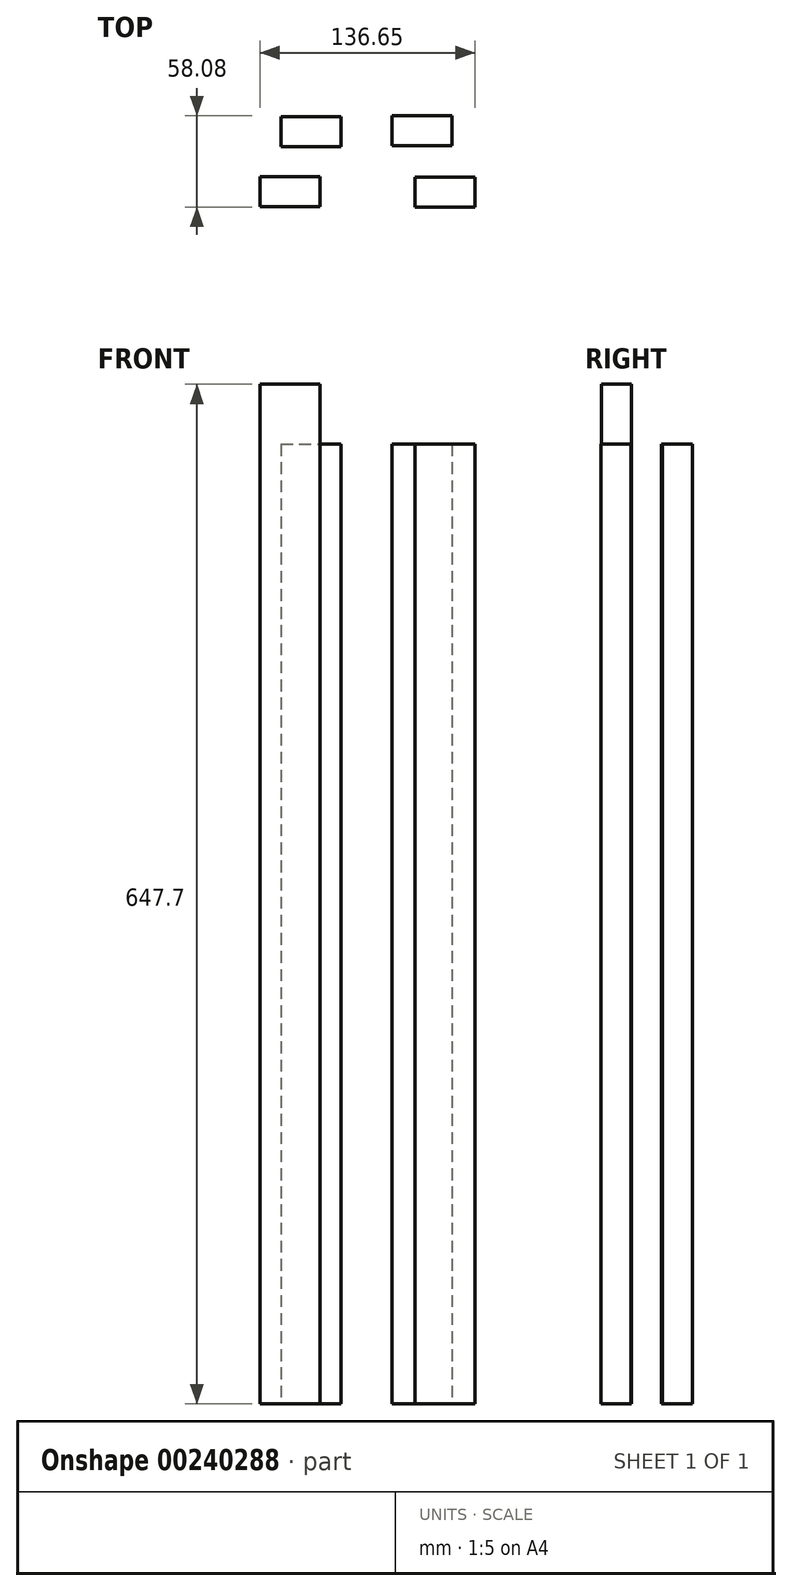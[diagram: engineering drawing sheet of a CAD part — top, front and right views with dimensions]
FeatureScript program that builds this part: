
annotation { "Feature Type Name" : "Feature", "Feature Type Description" : "" }
export const myFeature = defineFeature(function(context is Context, id is Id, definition is map)
    precondition{}
    {
        {
            var Q0;
            Q0=qCreatedBy(makeId("Top.planeOp"),FACE);
            var sketch = newSketch(context, id + "F0", { "sketchPlane" : qUnion([Q0])});
            skLineSegment(sketch, "E0.bottom", {"start": v(-65.46, 44.77) * mm, "end": v(-27.36, 44.77) * mm});
            skLineSegment(sketch, "E0.top", {"start": v(-65.46, 25.72) * mm, "end": v(-27.36, 25.72) * mm});
            skLineSegment(sketch, "E0.left", {"start": v(-65.46, 44.77) * mm, "end": v(-65.46, 25.72) * mm});
            skLineSegment(sketch, "E0.right", {"start": v(-27.36, 44.77) * mm, "end": v(-27.36, 25.72) * mm});
            skLineSegment(sketch, "E1.bottom", {"start": v(-78.98, 6.61) * mm, "end": v(-40.88, 6.61) * mm});
            skLineSegment(sketch, "E1.top", {"start": v(-78.98, -12.44) * mm, "end": v(-40.88, -12.44) * mm});
            skLineSegment(sketch, "E1.left", {"start": v(-78.98, 6.61) * mm, "end": v(-78.98, -12.44) * mm});
            skLineSegment(sketch, "E1.right", {"start": v(-40.88, 6.61) * mm, "end": v(-40.88, -12.44) * mm});
            skLineSegment(sketch, "E2.bottom", {"start": v(4.97, 45.36) * mm, "end": v(43.07, 45.36) * mm});
            skLineSegment(sketch, "E2.top", {"start": v(4.97, 26.3) * mm, "end": v(43.07, 26.3) * mm});
            skLineSegment(sketch, "E2.left", {"start": v(4.97, 45.36) * mm, "end": v(4.97, 26.3) * mm});
            skLineSegment(sketch, "E2.right", {"start": v(43.07, 45.36) * mm, "end": v(43.07, 26.3) * mm});
            skLineSegment(sketch, "E3.bottom", {"start": v(19.57, 6.33) * mm, "end": v(57.67, 6.33) * mm});
            skLineSegment(sketch, "E3.top", {"start": v(19.57, -12.72) * mm, "end": v(57.67, -12.72) * mm});
            skLineSegment(sketch, "E3.left", {"start": v(19.57, 6.33) * mm, "end": v(19.57, -12.72) * mm});
            skLineSegment(sketch, "E3.right", {"start": v(57.67, 6.33) * mm, "end": v(57.67, -12.72) * mm});
            skSolve(sketch);
        }
        {
            var Q0;
            Q0=makeQuery(id+"F0.imprint","IMPRINT",FACE,{"disambiguationData":[TD([[makeQuery(id+"F0.imprint","IMPRINT",EDGE,{"derivedFrom":sQuery(id+"F0.wireOp",EDGE,"E0.bottom")}),-1.0]])]});
            extrude(context, id + "F1", {"entities" : qUnion([Q0]), "depth" : 609.6 * mm});
        }
        {
            var Q0;
            Q0=makeQuery(id+"F0.imprint","IMPRINT",FACE,{"disambiguationData":[TD([[makeQuery(id+"F0.imprint","IMPRINT",EDGE,{"derivedFrom":sQuery(id+"F0.wireOp",EDGE,"E2.bottom")}),-1.0]])]});
            extrude(context, id + "F2", {"entities" : qUnion([Q0]), "depth" : 609.6 * mm});
        }
        {
            var Q0;
            Q0=makeQuery(id+"F0.imprint","IMPRINT",FACE,{"disambiguationData":[TD([[makeQuery(id+"F0.imprint","IMPRINT",EDGE,{"derivedFrom":sQuery(id+"F0.wireOp",EDGE,"E1.bottom")}),-1.0]])]});
            extrude(context, id + "F3", {"entities" : qUnion([Q0]), "depth" : 647.7 * mm});
        }
        {
            var Q0;
            Q0=makeQuery(id+"F0.imprint","IMPRINT",FACE,{"disambiguationData":[TD([[makeQuery(id+"F0.imprint","IMPRINT",EDGE,{"derivedFrom":sQuery(id+"F0.wireOp",EDGE,"E3.bottom")}),-1.0]])]});
            extrude(context, id + "F4", {"entities" : qUnion([Q0]), "depth" : 609.6 * mm});
        }
    });
